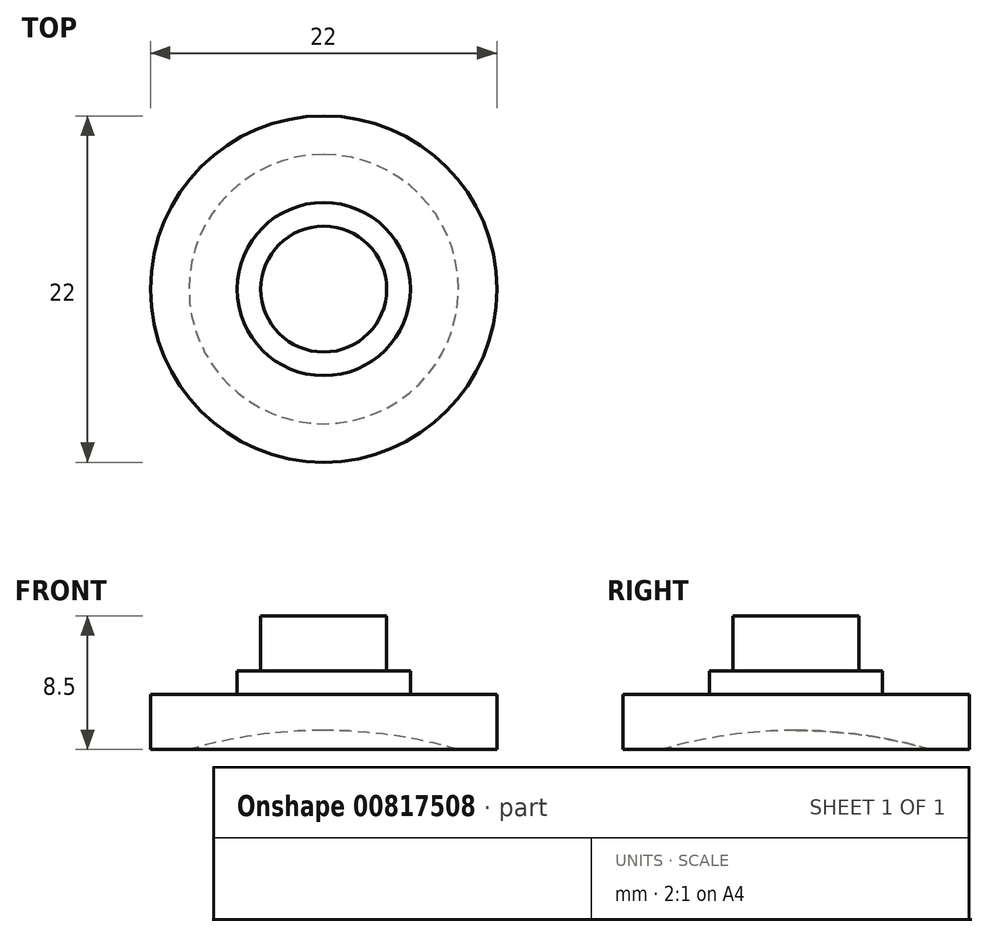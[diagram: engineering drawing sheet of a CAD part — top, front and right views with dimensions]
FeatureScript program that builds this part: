
annotation { "Feature Type Name" : "Feature", "Feature Type Description" : "" }
export const myFeature = defineFeature(function(context is Context, id is Id, definition is map)
    precondition{}
    {
        {
            var Q0;
            Q0=qCreatedBy(makeId("Top.planeOp"),FACE);
            var sketch = newSketch(context, id + "F0", { "sketchPlane" : qUnion([Q0])});
            skCircle(sketch, "E0", {"center": v(0, 0) * mm, "radius": 4 * mm});
            skCircle(sketch, "E1", {"center": v(0, 0) * mm, "radius": 11 * mm});
            skCircle(sketch, "E2", {"center": v(0, 0) * mm, "radius": 5.5 * mm});
            skSolve(sketch);
        }
        {
            var Q0;
            Q0=makeQuery(id+"F0.imprint","IMPRINT",FACE,{"disambiguationData":[TD([[makeQuery(id+"F0.imprint","IMPRINT",EDGE,{"derivedFrom":sQuery(id+"F0.wireOp",EDGE,"E0")}),1.0]])]});
            extrude(context, id + "F1", {"entities" : qUnion([Q0]), "depth" : 5 * mm, "offsetDistance" : 25.4 * mm});
        }
        {
            var Q0;
            Q0 = qSketchRegion(id + "F0", true);
            var Q1;
            Q1=makeQuery(id+"F0.imprint","IMPRINT",FACE,{"disambiguationData":[TD([[makeQuery(id+"F0.imprint","IMPRINT",EDGE,{"derivedFrom":sQuery(id+"F0.wireOp",EDGE,"E0")}),1.0]])]});
            var Q2;
            Q2=makeQuery(id+"F0.imprint","IMPRINT",FACE,{"disambiguationData":[TD([[makeQuery(id+"F0.imprint","IMPRINT",EDGE,{"derivedFrom":sQuery(id+"F0.wireOp",EDGE,"E0")}),-1.0]])]});
            extrude(context, id + "F2", {"entities" : qUnion([Q0, Q1, Q2]), "operationType" : NewBodyOperationType.ADD, "oppositeDirection" : true, "depth" : 3.5 * mm, "offsetDistance" : 25.4 * mm});
        }
        {
            var Q0;
            Q0=qCreatedBy(makeId("Right.planeOp"),FACE);
            var sketch = newSketch(context, id + "F3", { "sketchPlane" : qUnion([Q0])});
            skCircle(sketch, "E3", {"center": v(0, -33.02) * mm, "radius": 30.73 * mm});
            skLineSegment(sketch, "E4", {"start": v(0, -33.02) * mm, "end": v(0, 0) * mm});
            skLineSegment(sketch, "E5", {"start": v(0, -33.02) * mm, "end": v(0, -119.92) * mm});
            skSolve(sketch);
        }
        {
            var Q0;
            {var subQ0=sQuery(id+"F3.wireOp",EDGE,"E4");var subQ1=sQuery(id+"F3.wireOp",EDGE,"E3");var subQ2=makeQuery(id+"F3.imprint","INTERSECT",VERTEX,{"derivedFrom":[subQ1,subQ0]});Q0=makeQuery(id+"F3.imprint","IMPRINT",FACE,{"disambiguationData":[TD([[makeQuery(id+"F3.imprint","IMPRINT",EDGE,{"disambiguationData":[TD([[subQ2,-1.0]])],"derivedFrom":subQ1}),1.0]])]});}
            var Q1;
            Q1=sQuery(id+"F3.wireOp",EDGE,"E4");
            revolve(context, id + "F4", {"operationType" : NewBodyOperationType.REMOVE, "surfaceOperationType" : NewSurfaceOperationType.NEW, "entities" : qUnion([Q0]), "axis" : qUnion([Q1]), "revolveType" : RevolveType.FULL});
        }
        {
            var Q0;
            Q0=makeQuery(id+"F0.imprint","IMPRINT",FACE,{"disambiguationData":[TD([[makeQuery(id+"F0.imprint","IMPRINT",EDGE,{"derivedFrom":sQuery(id+"F0.wireOp",EDGE,"E0")}),-1.0]])]});
            extrude(context, id + "F5", {"entities" : qUnion([Q0]), "operationType" : NewBodyOperationType.ADD, "depth" : 1.5 * mm, "offsetDistance" : 25.4 * mm});
        }
    });
